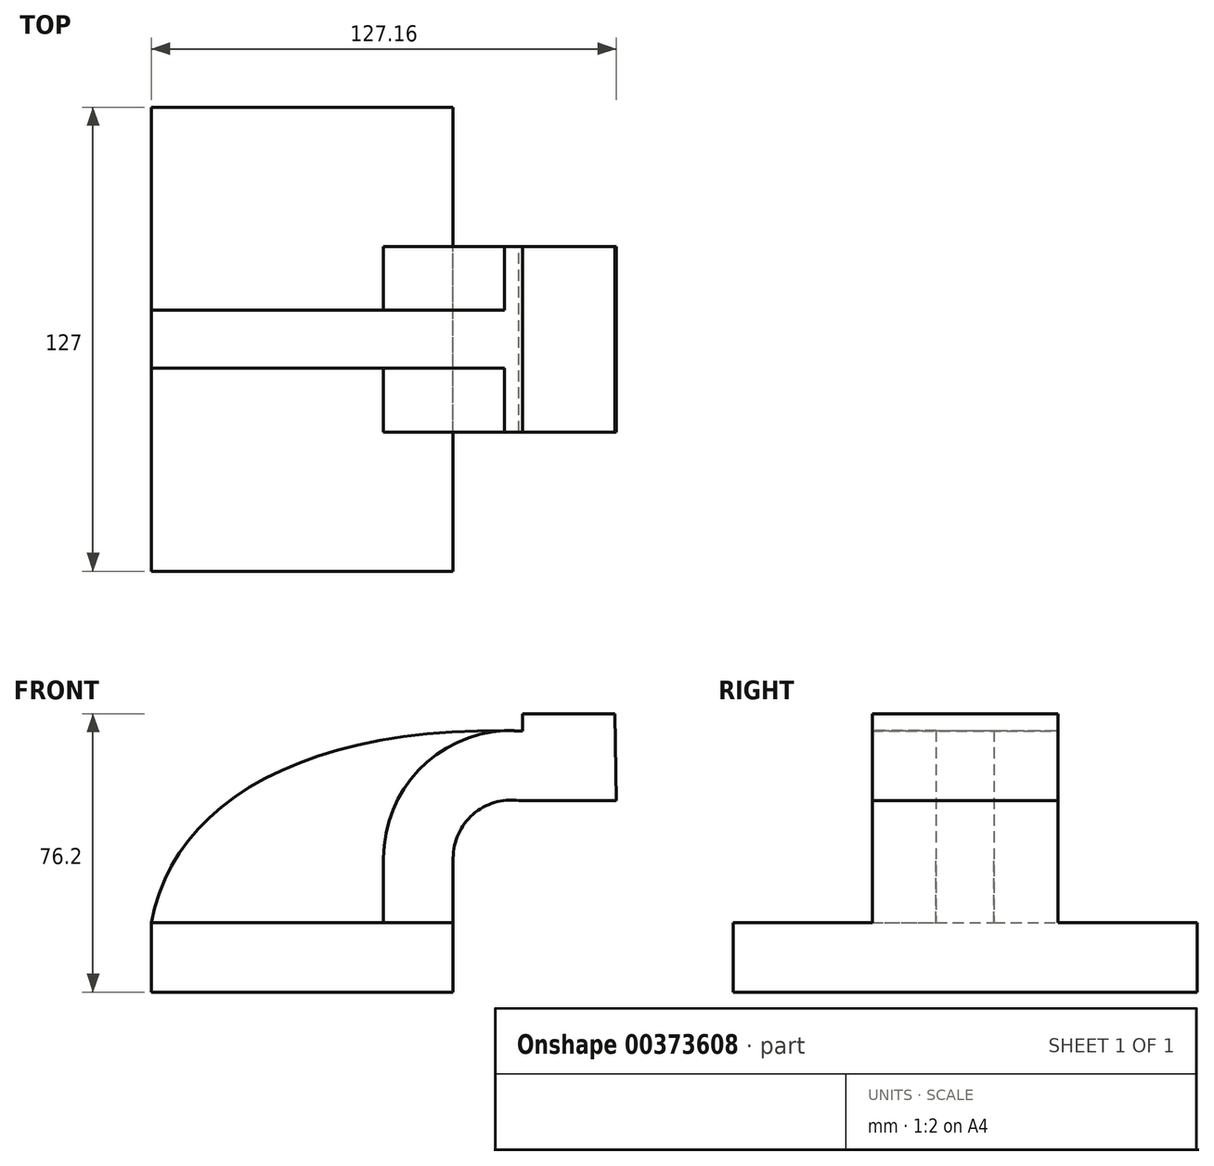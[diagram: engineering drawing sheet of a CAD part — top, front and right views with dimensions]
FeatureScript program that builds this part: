
annotation { "Feature Type Name" : "Feature", "Feature Type Description" : "" }
export const myFeature = defineFeature(function(context is Context, id is Id, definition is map)
    precondition{}
    {
        {
            var Q0;
            Q0=qCreatedBy(makeId("Front.planeOp"),FACE);
            var sketch = newSketch(context, id + "F0", { "sketchPlane" : qUnion([Q0])});
            skLineSegment(sketch, "E0.bottom", {"start": v(-41.28, -9.53) * mm, "end": v(41.28, -9.53) * mm});
            skLineSegment(sketch, "E0.top", {"start": v(-41.28, 9.53) * mm, "end": v(41.28, 9.53) * mm});
            skLineSegment(sketch, "E0.left", {"start": v(-41.28, -9.53) * mm, "end": v(-41.28, 9.53) * mm});
            skLineSegment(sketch, "E0.right", {"start": v(41.28, -9.53) * mm, "end": v(41.28, 9.52) * mm});
            skPoint(sketch, "E0.middle", {"position": v(0, 0) * mm});
            skLineSegment(sketch, "E1.bottom", {"start": v(111.12, 38.1) * mm, "end": v(60.33, 38.1) * mm});
            skLineSegment(sketch, "E1.top", {"start": v(111.13, 66.67) * mm, "end": v(60.33, 66.67) * mm});
            skLineSegment(sketch, "E1.left", {"start": v(111.13, 38.1) * mm, "end": v(111.13, 66.67) * mm});
            skLineSegment(sketch, "E1.right", {"start": v(60.33, 38.1) * mm, "end": v(60.33, 66.67) * mm});
            skPoint(sketch, "E1.middle", {"position": v(85.73, 52.39) * mm});
            skLineSegment(sketch, "E2", {"start": v(41.28, 9.52) * mm, "end": v(41.28, 27.14) * mm});
            skArc(sketch, "E3", {"start": v(41.27, 27.14) * mm, "mid": v(46.7, 39.1) * mm, "end": v(59.28, 42.88) * mm});
            skLineSegment(sketch, "E4", {"start": v(59.28, 42.88) * mm, "end": v(85.88, 42.88) * mm});
            skLineSegment(sketch, "E5.0", {"start": v(60.32, 61.93) * mm, "end": v(85.58, 61.93) * mm});
            skArc(sketch, "E5.1", {"start": v(22.23, 27.14) * mm, "mid": v(33.6, 52.94) * mm, "end": v(60.32, 61.93) * mm});
            skLineSegment(sketch, "E5.2", {"start": v(22.23, 9.52) * mm, "end": v(22.23, 27.14) * mm});
            skLineSegment(sketch, "E6", {"start": v(85.88, 42.88) * mm, "end": v(85.58, 66.67) * mm});
            skFitSpline(sketch, "E7", {"points": [v(60.32, 61.93) * mm, v(-41.28, 9.53) * mm], "startDerivative": vector(-180.96, 5.45) * mm, "endDerivative": vector(-16.9, -96.86) * mm});
            skSolve(sketch);
        }
        {
            var Q0;
            Q0=makeQuery(id+"F0.imprint","IMPRINT",FACE,{"disambiguationData":[TD([[makeQuery(id+"F0.imprint","IMPRINT",EDGE,{"derivedFrom":sQuery(id+"F0.wireOp",EDGE,"E0.bottom")}),1.0]])]});
            extrude(context, id + "F1", {"entities" : qUnion([Q0]), "endBound" : BoundingType.SYMMETRIC, "depth" : 127 * mm});
        }
        {
            var Q0;
            {var subQ1=sQuery(id+"F0.wireOp",EDGE,"E2");Q0=makeQuery(id+"F0.imprint","IMPRINT",FACE,{"disambiguationData":[TD([[makeQuery(id+"F0.imprint","IMPRINT",EDGE,{"derivedFrom":subQ1}),1.0]])]});}
            var Q1;
            {var subQ4=sQuery(id+"F0.wireOp",EDGE,"E6");Q1=makeQuery(id+"F0.imprint","IMPRINT",FACE,{"disambiguationData":[TD([[makeQuery(id+"F0.imprint","IMPRINT",EDGE,{"derivedFrom":subQ4}),1.0]])]});}
            extrude(context, id + "F2", {"entities" : qUnion([Q0, Q1]), "operationType" : NewBodyOperationType.ADD, "endBound" : BoundingType.SYMMETRIC, "depth" : 50.8 * mm});
        }
        {
            var Q0;
            {var subQ3=sQuery(id+"F0.wireOp",EDGE,"E5.2");Q0=makeQuery(id+"F0.imprint","IMPRINT",FACE,{"disambiguationData":[TD([[makeQuery(id+"F0.imprint","IMPRINT",EDGE,{"derivedFrom":subQ3}),1.0]])]});}
            extrude(context, id + "F3", {"entities" : qUnion([Q0]), "operationType" : NewBodyOperationType.ADD, "endBound" : BoundingType.SYMMETRIC, "depth" : 15.88 * mm});
        }
    });
